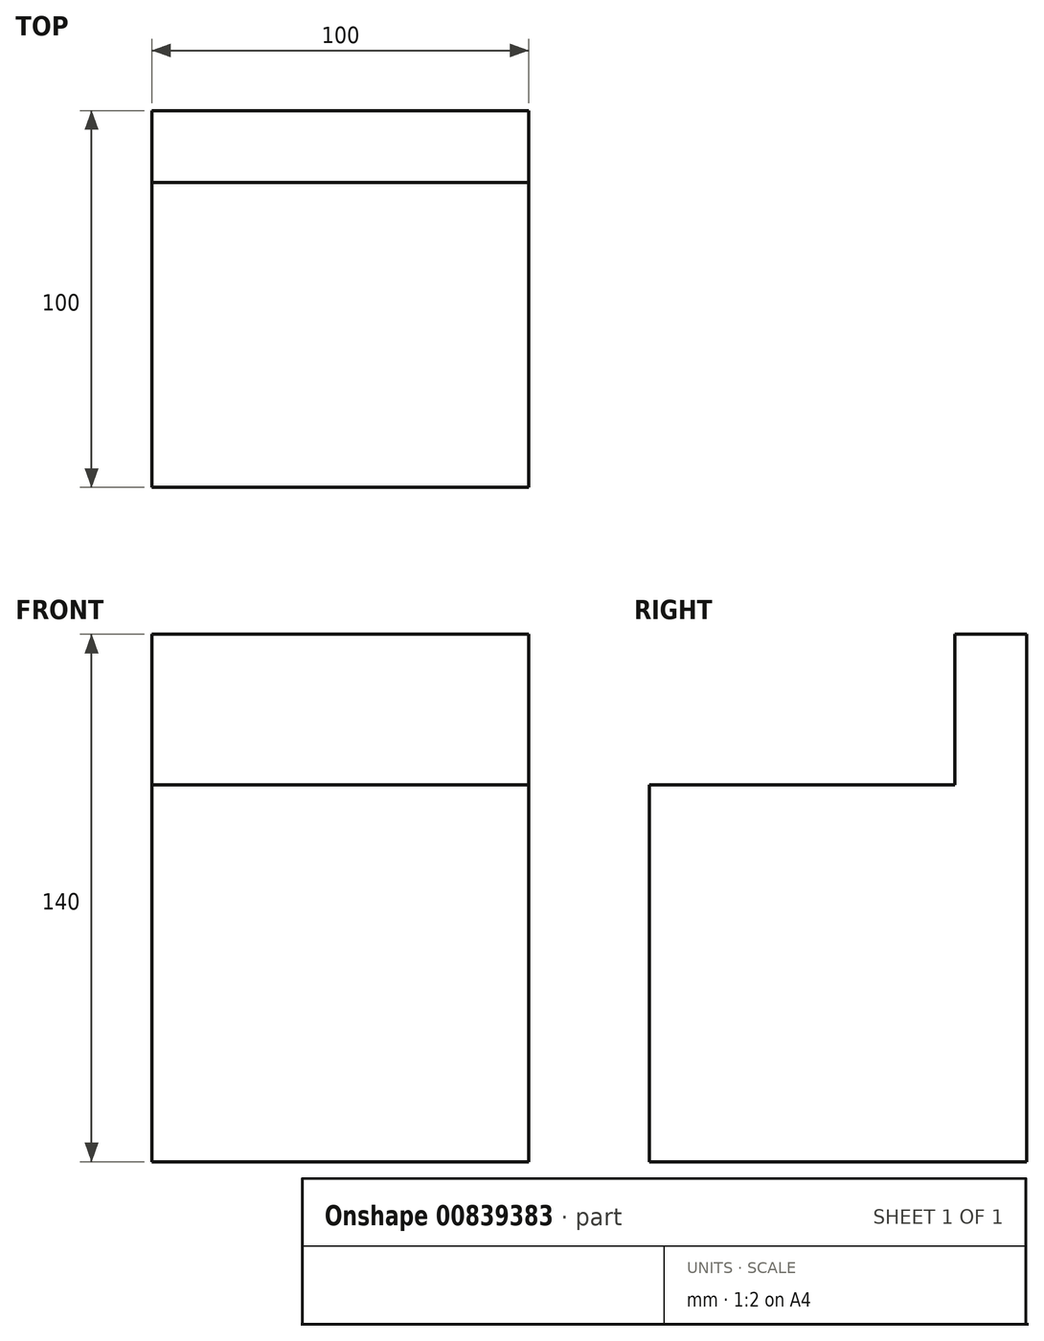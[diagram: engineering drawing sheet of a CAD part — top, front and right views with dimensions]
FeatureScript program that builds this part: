
annotation { "Feature Type Name" : "Feature", "Feature Type Description" : "" }
export const myFeature = defineFeature(function(context is Context, id is Id, definition is map)
    precondition{}
    {
        {
            var Q0;
            Q0=qCreatedBy(makeId("Top.planeOp"),FACE);
            var sketch = newSketch(context, id + "F0", { "sketchPlane" : qUnion([Q0])});
            skLineSegment(sketch, "E0.bottom", {"start": v(-50, 50) * mm, "end": v(50, 50) * mm});
            skLineSegment(sketch, "E0.top", {"start": v(-50, -50) * mm, "end": v(50, -50) * mm});
            skLineSegment(sketch, "E0.left", {"start": v(-50, 50) * mm, "end": v(-50, -50) * mm});
            skLineSegment(sketch, "E0.right", {"start": v(50, 50) * mm, "end": v(50, -50) * mm});
            skPoint(sketch, "E0.middle", {"position": v(0, 0) * mm});
            skSolve(sketch);
        }
        {
            var Q0;
            Q0 = qSketchRegion(id + "F0", true);
            extrude(context, id + "F1", {"entities" : qUnion([Q0]), "depth" : 100 * mm, "offsetDistance" : 25 * mm});
        }
        {
            var Q0;
            Q0=makeQuery(id+"F1.opExtrude","CAP_FACE",FACE,{"disambiguationData":[OSD([sQuery(id+"F0.wireOp",EDGE,"E0.bottom"),sQuery(id+"F0.wireOp",EDGE,"E0.top"),sQuery(id+"F0.wireOp",EDGE,"E0.left"),sQuery(id+"F0.wireOp",EDGE,"E0.right")])],"isStart":false});
            var sketch = newSketch(context, id + "F2", { "sketchPlane" : qUnion([Q0])});
            skLineSegment(sketch, "E1.bottom", {"start": v(50, -50) * mm, "end": v(-50, -50) * mm});
            skLineSegment(sketch, "E1.top", {"start": v(50, 30.98) * mm, "end": v(-50, 30.98) * mm});
            skLineSegment(sketch, "E1.left", {"start": v(50, -50) * mm, "end": v(50, 30.98) * mm});
            skLineSegment(sketch, "E1.right", {"start": v(-50, -50) * mm, "end": v(-50, 30.98) * mm});
            skSolve(sketch);
        }
        {
            var Q0;
            {var subQ0=sQuery(id+"F2.wireOp",EDGE,"E1.top");Q0=makeQuery(id+"F2.imprint","IMPRINT",FACE,{"disambiguationData":[TD([[makeQuery(id+"F2.imprint","IMPRINT",EDGE,{"derivedFrom":subQ0}),-1.0]])]});}
            extrude(context, id + "F3", {"entities" : qUnion([Q0]), "operationType" : NewBodyOperationType.ADD, "depth" : 40 * mm, "offsetDistance" : 25 * mm});
        }
    });
